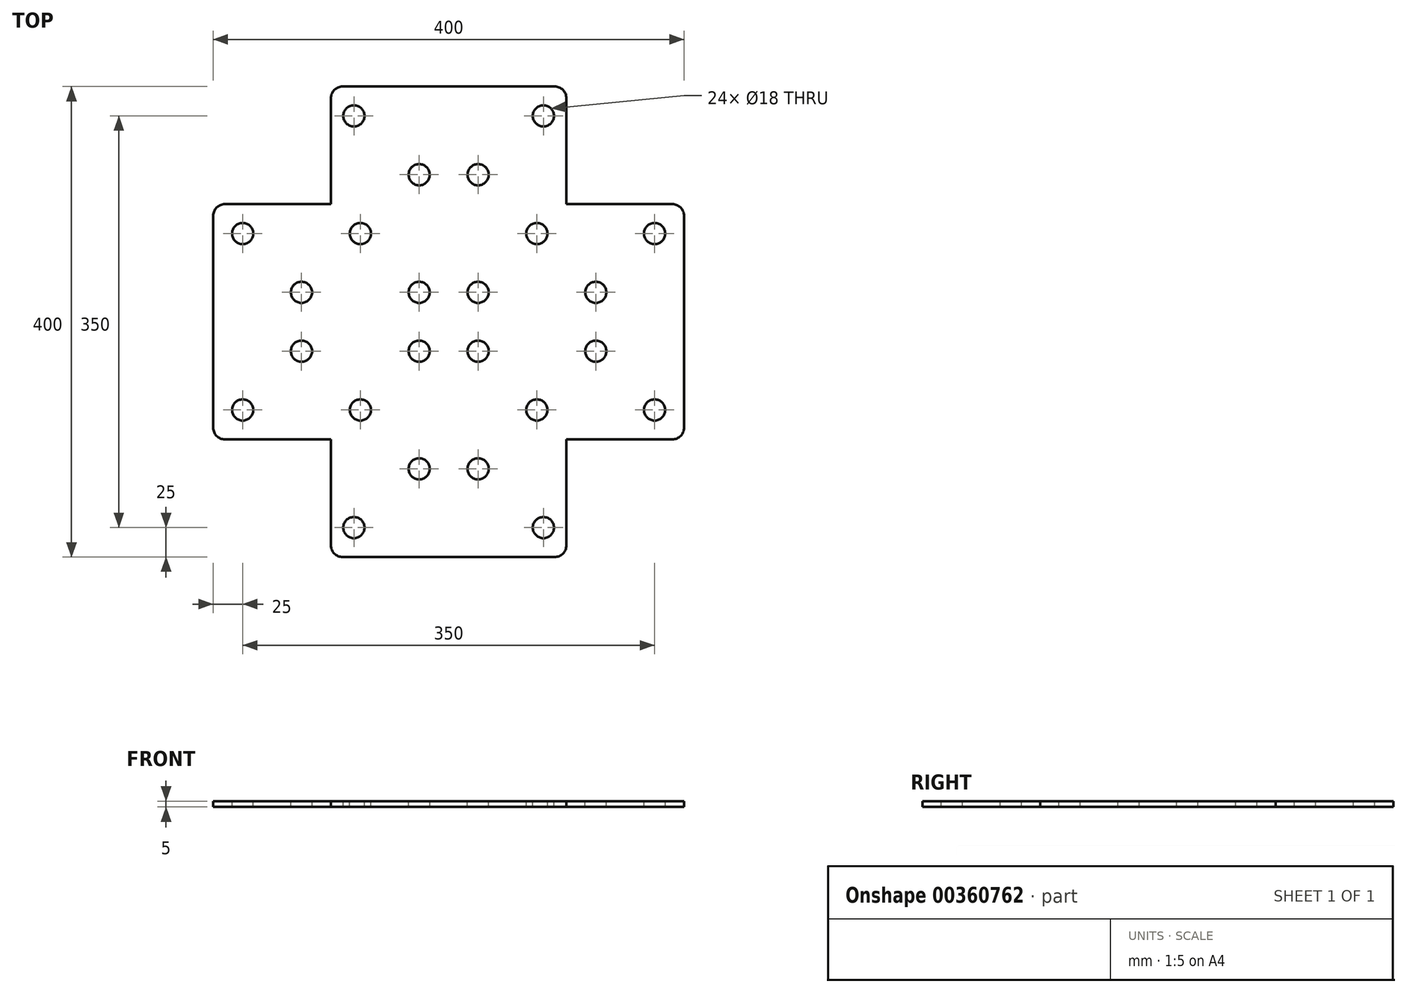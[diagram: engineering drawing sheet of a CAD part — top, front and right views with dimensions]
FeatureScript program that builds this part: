
annotation { "Feature Type Name" : "Feature", "Feature Type Description" : "" }
export const myFeature = defineFeature(function(context is Context, id is Id, definition is map)
    precondition{}
    {
        {
            var Q0;
            Q0=qCreatedBy(makeId("Top.planeOp"),FACE);
            var sketch = newSketch(context, id + "F0", { "sketchPlane" : qUnion([Q0])});
            skLineSegment(sketch, "E0", {"start": v(0, -200) * mm, "end": v(100, -200) * mm});
            skLineSegment(sketch, "E1", {"start": v(100, -200) * mm, "end": v(100, -100) * mm});
            skLineSegment(sketch, "E2", {"start": v(100, -100) * mm, "end": v(200, -100) * mm});
            skLineSegment(sketch, "E3", {"start": v(200, -100) * mm, "end": v(200, 0) * mm});
            skLineSegment(sketch, "E4.MirrorCS", {"start": v(100, 200) * mm, "end": v(100, 100) * mm});
            skLineSegment(sketch, "E5.MirrorCS", {"start": v(0, 200) * mm, "end": v(100, 200) * mm});
            skLineSegment(sketch, "E6.MirrorCS", {"start": v(100, 100) * mm, "end": v(200, 100) * mm});
            skLineSegment(sketch, "E7.MirrorCS", {"start": v(200, 100) * mm, "end": v(200, 0) * mm});
            skLineSegment(sketch, "E8.MirrorCS", {"start": v(0, -200) * mm, "end": v(-100, -200) * mm});
            skLineSegment(sketch, "E9.MirrorCS", {"start": v(-100, -200) * mm, "end": v(-100, -100) * mm});
            skLineSegment(sketch, "E10.MirrorCS", {"start": v(-100, -100) * mm, "end": v(-200, -100) * mm});
            skLineSegment(sketch, "E11.MirrorCS", {"start": v(-100, 100) * mm, "end": v(-200, 100) * mm});
            skLineSegment(sketch, "E12.MirrorCS", {"start": v(-200, 100) * mm, "end": v(-200, 0) * mm});
            skLineSegment(sketch, "E13.MirrorCS", {"start": v(-200, -100) * mm, "end": v(-200, 0) * mm});
            skLineSegment(sketch, "E14.MirrorCS", {"start": v(-100, 200) * mm, "end": v(-100, 100) * mm});
            skLineSegment(sketch, "E15.MirrorCS", {"start": v(0, 200) * mm, "end": v(-100, 200) * mm});
            skSolve(sketch);
        }
        {
            var Q0;
            Q0=makeQuery(id+"F0.imprint","IMPRINT",FACE,{"disambiguationData":[TD([[makeQuery(id+"F0.imprint","IMPRINT",EDGE,{"derivedFrom":sQuery(id+"F0.wireOp",EDGE,"E0")}),1.0]])]});
            extrude(context, id + "F1", {"entities" : qUnion([Q0]), "depth" : 5 * mm});
        }
        {
            var Q0;
            Q0=makeQuery(id+"F1.opExtrude","CAP_FACE",FACE,{"disambiguationData":[OSD([sQuery(id+"F0.wireOp",EDGE,"E0"),sQuery(id+"F0.wireOp",EDGE,"E1"),sQuery(id+"F0.wireOp",EDGE,"E2"),sQuery(id+"F0.wireOp",EDGE,"E3"),sQuery(id+"F0.wireOp",EDGE,"E4.MirrorCS"),sQuery(id+"F0.wireOp",EDGE,"E5.MirrorCS"),sQuery(id+"F0.wireOp",EDGE,"E6.MirrorCS"),sQuery(id+"F0.wireOp",EDGE,"E7.MirrorCS"),sQuery(id+"F0.wireOp",EDGE,"E8.MirrorCS"),sQuery(id+"F0.wireOp",EDGE,"E9.MirrorCS"),sQuery(id+"F0.wireOp",EDGE,"E10.MirrorCS"),sQuery(id+"F0.wireOp",EDGE,"E11.MirrorCS"),sQuery(id+"F0.wireOp",EDGE,"E12.MirrorCS"),sQuery(id+"F0.wireOp",EDGE,"E13.MirrorCS"),sQuery(id+"F0.wireOp",EDGE,"E14.MirrorCS"),sQuery(id+"F0.wireOp",EDGE,"E15.MirrorCS")])],"isStart":false});
            var sketch = newSketch(context, id + "F2", { "sketchPlane" : qUnion([Q0])});
            skCircle(sketch, "E16", {"center": v(25, 25) * mm, "radius": 9 * mm});
            skCircle(sketch, "E17.1.1.0", {"center": v(75, 75) * mm, "radius": 9 * mm});
            skCircle(sketch, "E17.2.0.0", {"center": v(125, 25) * mm, "radius": 9 * mm});
            skCircle(sketch, "E17.3.1.0", {"center": v(175, 75) * mm, "radius": 9 * mm});
            skCircle(sketch, "E18.0.1.1", {"center": v(25, 125) * mm, "radius": 9 * mm});
            skCircle(sketch, "E18.0.1.4", {"center": v(80.5, 175) * mm, "radius": 9 * mm});
            skCircle(sketch, "E19.MirrorC", {"center": v(80.5, -175) * mm, "radius": 9 * mm});
            skCircle(sketch, "E20.MirrorC", {"center": v(25, -125) * mm, "radius": 9 * mm});
            skCircle(sketch, "E21.MirrorC", {"center": v(175, -75) * mm, "radius": 9 * mm});
            skCircle(sketch, "E22.MirrorC", {"center": v(75, -75) * mm, "radius": 9 * mm});
            skCircle(sketch, "E23.MirrorC", {"center": v(125, -25) * mm, "radius": 9 * mm});
            skCircle(sketch, "E24.MirrorC", {"center": v(25, -25) * mm, "radius": 9 * mm});
            skCircle(sketch, "E25.MirrorC", {"center": v(-25, -125) * mm, "radius": 9 * mm});
            skCircle(sketch, "E26.MirrorC", {"center": v(-175, 75) * mm, "radius": 9 * mm});
            skCircle(sketch, "E27.MirrorC", {"center": v(-175, -75) * mm, "radius": 9 * mm});
            skCircle(sketch, "E28.MirrorC", {"center": v(-80.5, 175) * mm, "radius": 9 * mm});
            skCircle(sketch, "E29.MirrorC", {"center": v(-25, 25) * mm, "radius": 9 * mm});
            skCircle(sketch, "E30.MirrorC", {"center": v(-125, 25) * mm, "radius": 9 * mm});
            skCircle(sketch, "E31.MirrorC", {"center": v(-125, -25) * mm, "radius": 9 * mm});
            skCircle(sketch, "E32.MirrorC", {"center": v(-80.5, -175) * mm, "radius": 9 * mm});
            skCircle(sketch, "E33.MirrorC", {"center": v(-25, -25) * mm, "radius": 9 * mm});
            skCircle(sketch, "E34.MirrorC", {"center": v(-25, 125) * mm, "radius": 9 * mm});
            skCircle(sketch, "E35.MirrorC", {"center": v(-75, 75) * mm, "radius": 9 * mm});
            skCircle(sketch, "E36.MirrorC", {"center": v(-75, -75) * mm, "radius": 9 * mm});
            skSolve(sketch);
        }
        {
            var Q0;
            Q0=qSketchRegion(id+"F2",true);
            extrude(context, id + "F3", {"entities" : qUnion([Q0]), "operationType" : NewBodyOperationType.REMOVE, "oppositeDirection" : true, "depth" : 25 * mm});
        }
        {
            var Q0;
            Q0=makeQuery(id+"F1.opExtrude","SWEPT_EDGE",EDGE,{"disambiguationData":[OSD([sQuery(id+"F0.wireOp",EDGE,"E0"),sQuery(id+"F0.wireOp",EDGE,"E1")])]});
            var Q1;
            Q1=makeQuery(id+"F1.opExtrude","SWEPT_EDGE",EDGE,{"disambiguationData":[OSD([sQuery(id+"F0.wireOp",EDGE,"E8.MirrorCS"),sQuery(id+"F0.wireOp",EDGE,"E9.MirrorCS")])]});
            var Q2;
            Q2=makeQuery(id+"F1.opExtrude","SWEPT_EDGE",EDGE,{"disambiguationData":[OSD([sQuery(id+"F0.wireOp",EDGE,"E10.MirrorCS"),sQuery(id+"F0.wireOp",EDGE,"E13.MirrorCS")])]});
            var Q3;
            Q3=makeQuery(id+"F1.opExtrude","SWEPT_EDGE",EDGE,{"disambiguationData":[OSD([sQuery(id+"F0.wireOp",EDGE,"E11.MirrorCS"),sQuery(id+"F0.wireOp",EDGE,"E12.MirrorCS")])]});
            var Q4;
            Q4=makeQuery(id+"F1.opExtrude","SWEPT_EDGE",EDGE,{"disambiguationData":[OSD([sQuery(id+"F0.wireOp",EDGE,"E14.MirrorCS"),sQuery(id+"F0.wireOp",EDGE,"E15.MirrorCS")])]});
            var Q5;
            Q5=makeQuery(id+"F1.opExtrude","SWEPT_EDGE",EDGE,{"disambiguationData":[OSD([sQuery(id+"F0.wireOp",EDGE,"E4.MirrorCS"),sQuery(id+"F0.wireOp",EDGE,"E5.MirrorCS")])]});
            var Q6;
            Q6=makeQuery(id+"F1.opExtrude","SWEPT_EDGE",EDGE,{"disambiguationData":[OSD([sQuery(id+"F0.wireOp",EDGE,"E6.MirrorCS"),sQuery(id+"F0.wireOp",EDGE,"E7.MirrorCS")])]});
            var Q7;
            Q7=makeQuery(id+"F1.opExtrude","SWEPT_EDGE",EDGE,{"disambiguationData":[OSD([sQuery(id+"F0.wireOp",EDGE,"E2"),sQuery(id+"F0.wireOp",EDGE,"E3")])]});
            fillet(context, id + "F4", {"entities" : qUnion([Q0, Q1, Q2, Q3, Q4, Q5, Q6, Q7]), "radius" : 10 * mm, "tangentPropagation" : true, "allowEdgeOverflow" : false});
        }
    });
